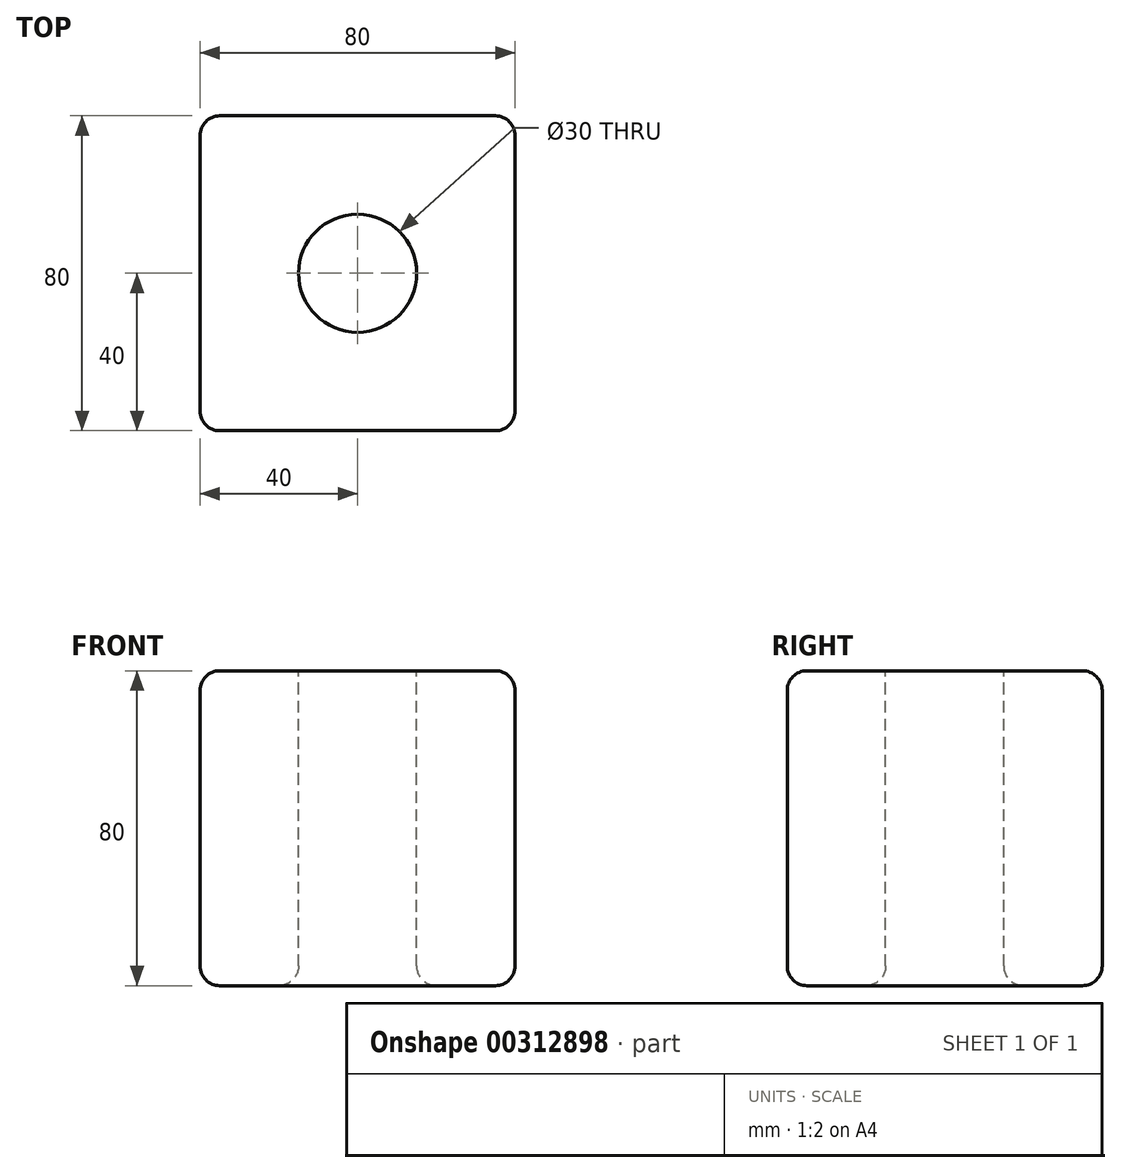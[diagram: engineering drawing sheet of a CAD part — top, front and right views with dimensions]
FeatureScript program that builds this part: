
annotation { "Feature Type Name" : "Feature", "Feature Type Description" : "" }
export const myFeature = defineFeature(function(context is Context, id is Id, definition is map)
    precondition{}
    {
        {
            var Q0;
            Q0=qCreatedBy(makeId("Top.planeOp"),FACE);
            var sketch = newSketch(context, id + "F0", { "sketchPlane" : qUnion([Q0])});
            skLineSegment(sketch, "E0.bottom", {"start": v(-40, 40) * mm, "end": v(40, 40) * mm});
            skLineSegment(sketch, "E0.top", {"start": v(-40, -40) * mm, "end": v(40, -40) * mm});
            skLineSegment(sketch, "E0.left", {"start": v(-40, 40) * mm, "end": v(-40, -40) * mm});
            skLineSegment(sketch, "E0.right", {"start": v(40, 40) * mm, "end": v(40, -40) * mm});
            skPoint(sketch, "E0.middle", {"position": v(0, 0) * mm});
            skSolve(sketch);
        }
        {
            var Q0;
            Q0 = qSketchRegion(id + "F0", true);
            extrude(context, id + "F1", {"entities" : qUnion([Q0]), "depth" : 80 * mm});
        }
        {
            var Q0;
            Q0=makeQuery(id+"F1.opExtrude","CAP_EDGE",EDGE,{"disambiguationData":[OSD([sQuery(id+"F0.wireOp",EDGE,"E0.bottom")])],"isStart":false});
            var Q1;
            Q1=makeQuery(id+"F1.opExtrude","CAP_EDGE",EDGE,{"disambiguationData":[OSD([sQuery(id+"F0.wireOp",EDGE,"E0.left")])],"isStart":false});
            var Q2;
            Q2=makeQuery(id+"F1.opExtrude","CAP_EDGE",EDGE,{"disambiguationData":[OSD([sQuery(id+"F0.wireOp",EDGE,"E0.right")])],"isStart":false});
            var Q3;
            Q3=makeQuery(id+"F1.opExtrude","CAP_EDGE",EDGE,{"disambiguationData":[OSD([sQuery(id+"F0.wireOp",EDGE,"E0.top")])],"isStart":false});
            var Q4;
            Q4=makeQuery(id+"F1.opExtrude","SWEPT_EDGE",EDGE,{"disambiguationData":[OSD([sQuery(id+"F0.wireOp",EDGE,"E0.top"),sQuery(id+"F0.wireOp",EDGE,"E0.right")])]});
            var Q5;
            Q5=makeQuery(id+"F1.opExtrude","CAP_EDGE",EDGE,{"disambiguationData":[OSD([sQuery(id+"F0.wireOp",EDGE,"E0.top")])],"isStart":true});
            var Q6;
            Q6=makeQuery(id+"F1.opExtrude","SWEPT_EDGE",EDGE,{"disambiguationData":[OSD([sQuery(id+"F0.wireOp",EDGE,"E0.top"),sQuery(id+"F0.wireOp",EDGE,"E0.left")])]});
            var Q7;
            Q7=makeQuery(id+"F1.opExtrude","CAP_EDGE",EDGE,{"disambiguationData":[OSD([sQuery(id+"F0.wireOp",EDGE,"E0.right")])],"isStart":true});
            var Q8;
            Q8=makeQuery(id+"F1.opExtrude","SWEPT_EDGE",EDGE,{"disambiguationData":[OSD([sQuery(id+"F0.wireOp",EDGE,"E0.bottom"),sQuery(id+"F0.wireOp",EDGE,"E0.left")])]});
            var Q9;
            Q9=makeQuery(id+"F1.opExtrude","CAP_EDGE",EDGE,{"disambiguationData":[OSD([sQuery(id+"F0.wireOp",EDGE,"E0.left")])],"isStart":true});
            var Q10;
            Q10=makeQuery(id+"F1.opExtrude","CAP_EDGE",EDGE,{"disambiguationData":[OSD([sQuery(id+"F0.wireOp",EDGE,"E0.bottom")])],"isStart":true});
            var Q11;
            Q11=makeQuery(id+"F1.opExtrude","SWEPT_EDGE",EDGE,{"disambiguationData":[OSD([sQuery(id+"F0.wireOp",EDGE,"E0.bottom"),sQuery(id+"F0.wireOp",EDGE,"E0.right")])]});
            fillet(context, id + "F2", {"entities" : qUnion([Q0, Q1, Q2, Q3, Q4, Q5, Q6, Q7, Q8, Q9, Q10, Q11]), "radius" : 5 * mm, "tangentPropagation" : true, "allowEdgeOverflow" : false});
        }
        {
            var Q0;
            Q0=makeQuery(id+"F1.opExtrude","CAP_FACE",FACE,{"disambiguationData":[OSD([sQuery(id+"F0.wireOp",EDGE,"E0.bottom"),sQuery(id+"F0.wireOp",EDGE,"E0.top"),sQuery(id+"F0.wireOp",EDGE,"E0.left"),sQuery(id+"F0.wireOp",EDGE,"E0.right")])],"isStart":false});
            var sketch = newSketch(context, id + "F3", { "sketchPlane" : qUnion([Q0])});
            skCircle(sketch, "E1", {"center": v(0, 0) * mm, "radius": 15 * mm});
            skSolve(sketch);
        }
        {
            var Q0;
            Q0 = qSketchRegion(id + "F3", true);
            extrude(context, id + "F4", {"entities" : qUnion([Q0]), "operationType" : NewBodyOperationType.REMOVE, "endBound" : BoundingType.THROUGH_ALL, "oppositeDirection" : true, "depth" : 25 * mm});
        }
        {
            var Q0;
            Q0=makeQuery(id+"F4.boolean.opBoolean","COPY",EDGE,{"derivedFrom":makeQuery(id+"F4.opExtrude","CAP_EDGE",EDGE,{"disambiguationData":[OSD([sQuery(id+"F3.wireOp",EDGE,"E1")])],"isStart":true})});
            var Q1;
            Q1=makeQuery(id+"F4.boolean.opBoolean","INTERSECT",EDGE,{"derivedFrom":[makeQuery(id+"F1.opExtrude","CAP_FACE",FACE,{"disambiguationData":[OSD([sQuery(id+"F0.wireOp",EDGE,"E0.bottom"),sQuery(id+"F0.wireOp",EDGE,"E0.top"),sQuery(id+"F0.wireOp",EDGE,"E0.left"),sQuery(id+"F0.wireOp",EDGE,"E0.right")])],"isStart":true}),makeQuery(id+"F4.opExtrude","SWEPT_FACE",FACE,{"disambiguationData":[OSD([sQuery(id+"F3.wireOp",EDGE,"E1")])]})]});
            fillet(context, id + "F5", {"entities" : qUnion([Q0, Q1]), "radius" : 5 * mm, "tangentPropagation" : true, "allowEdgeOverflow" : false});
        }
    });
